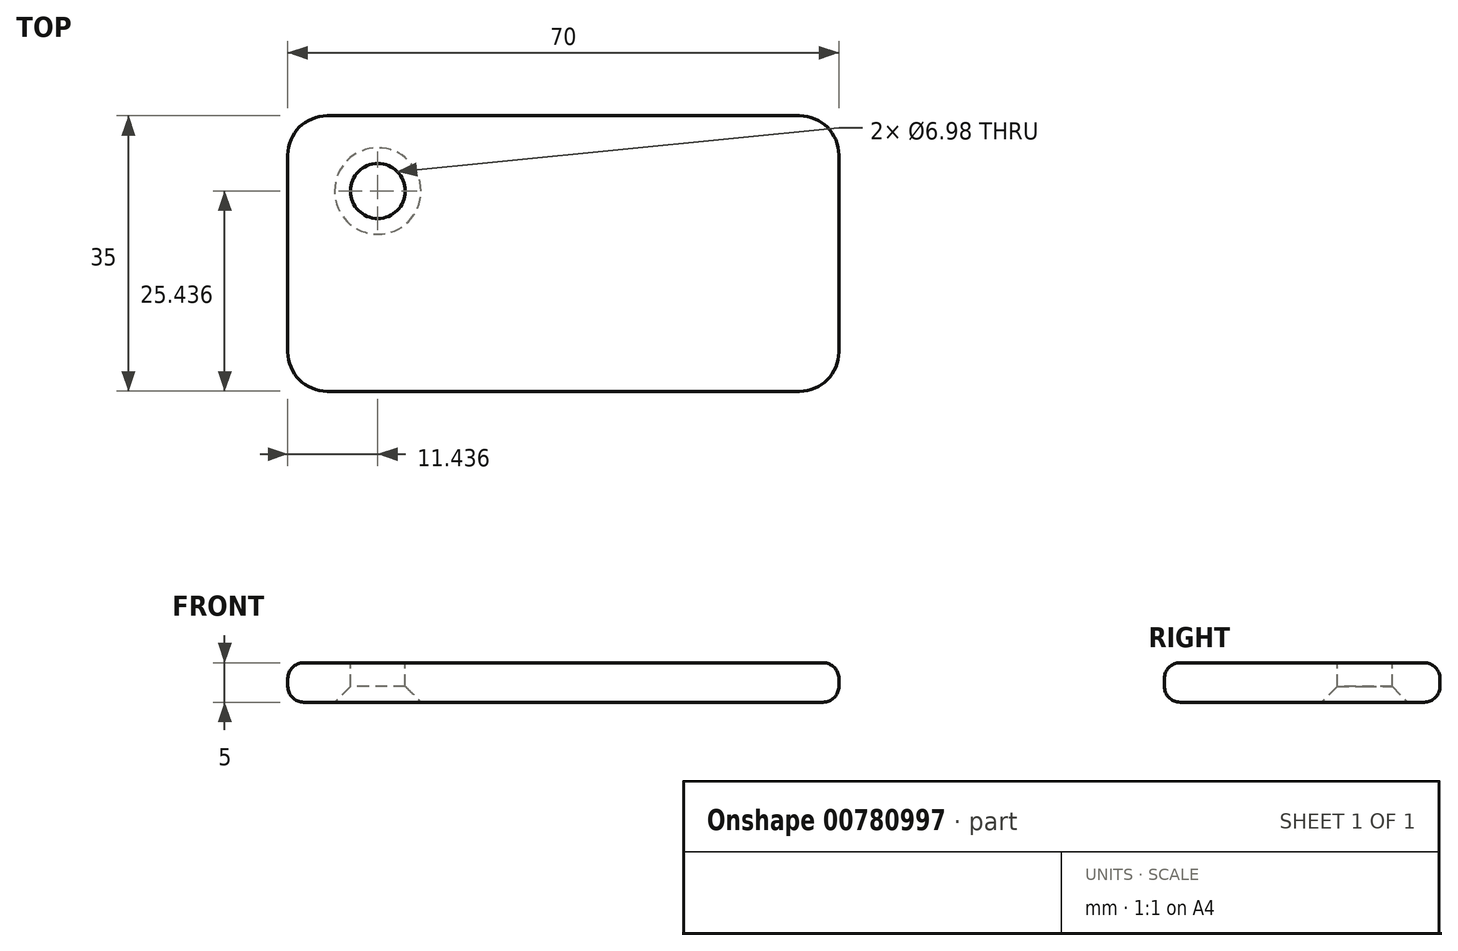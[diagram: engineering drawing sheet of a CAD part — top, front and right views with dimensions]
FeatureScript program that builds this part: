
annotation { "Feature Type Name" : "Feature", "Feature Type Description" : "" }
export const myFeature = defineFeature(function(context is Context, id is Id, definition is map)
    precondition{}
    {
        {
            var Q0;
            Q0=qCreatedBy(makeId("Top.planeOp"),FACE);
            var sketch = newSketch(context, id + "F0", { "sketchPlane" : qUnion([Q0])});
            skLineSegment(sketch, "E0.bottom", {"start": v(15.7, -5.3) * mm, "end": v(-44.3, -5.3) * mm});
            skLineSegment(sketch, "E0.top", {"start": v(15.7, -40.3) * mm, "end": v(-44.3, -40.3) * mm});
            skLineSegment(sketch, "E0.left", {"start": v(20.7, -10.3) * mm, "end": v(20.7, -35.3) * mm});
            skLineSegment(sketch, "E0.right", {"start": v(-49.3, -10.3) * mm, "end": v(-49.3, -35.3) * mm});
            skPoint(sketch, "E0.middle", {"position": v(-14.3, -22.8) * mm});
            skPoint(sketch, "E1.right.end.orphan", {"position": v(-3.57, 0) * mm});
            skPoint(sketch, "E2.visualSharp", {"position": v(20.7, -5.3) * mm});
            skArc(sketch, "E2.filletArc", {"start": v(20.7, -10.3) * mm, "mid": v(19.23, -6.77) * mm, "end": v(15.7, -5.3) * mm});
            skPoint(sketch, "E3.visualSharp", {"position": v(-49.3, -5.3) * mm});
            skArc(sketch, "E3.filletArc", {"start": v(-44.3, -5.3) * mm, "mid": v(-47.84, -6.77) * mm, "end": v(-49.3, -10.3) * mm});
            skPoint(sketch, "E4.visualSharp", {"position": v(-49.3, -40.3) * mm});
            skArc(sketch, "E4.filletArc", {"start": v(-49.3, -35.3) * mm, "mid": v(-47.84, -38.84) * mm, "end": v(-44.3, -40.3) * mm});
            skPoint(sketch, "E5.visualSharp", {"position": v(20.7, -40.3) * mm});
            skArc(sketch, "E5.filletArc", {"start": v(15.7, -40.3) * mm, "mid": v(19.23, -38.84) * mm, "end": v(20.7, -35.3) * mm});
            skSolve(sketch);
        }
        {
            var Q0;
            Q0=makeQuery(id+"F0.imprint","IMPRINT",FACE,{"disambiguationData":[TD([[makeQuery(id+"F0.imprint","IMPRINT",EDGE,{"derivedFrom":sQuery(id+"F0.wireOp",EDGE,"E0.bottom")}),1.0]])]});
            extrude(context, id + "F1", {"entities" : qUnion([Q0]), "depth" : 5 * mm, "offsetDistance" : 25 * mm});
        }
        {
            var Q0;
            Q0=makeQuery(id+"F1.opExtrude","CAP_EDGE",EDGE,{"disambiguationData":[OSD([sQuery(id+"F0.wireOp",EDGE,"E0.right")])],"isStart":false});
            var Q1;
            Q1=makeQuery(id+"F1.opExtrude","CAP_EDGE",EDGE,{"disambiguationData":[OSD([sQuery(id+"F0.wireOp",EDGE,"E0.right")])],"isStart":true});
            fillet(context, id + "F2", {"entities" : qUnion([Q0, Q1]), "radius" : 2 * mm, "tangentPropagation" : true, "allowEdgeOverflow" : false});
        }
        {
            var Q0;
            Q0=makeQuery(id+"F1.opExtrude","CAP_FACE",FACE,{"disambiguationData":[OSD([sQuery(id+"F0.wireOp",EDGE,"E0.bottom"),sQuery(id+"F0.wireOp",EDGE,"E0.top"),sQuery(id+"F0.wireOp",EDGE,"E0.left"),sQuery(id+"F0.wireOp",EDGE,"E0.right"),sQuery(id+"F0.wireOp",EDGE,"E2.filletArc"),sQuery(id+"F0.wireOp",EDGE,"E3.filletArc"),sQuery(id+"F0.wireOp",EDGE,"E4.filletArc"),sQuery(id+"F0.wireOp",EDGE,"E5.filletArc")])],"isStart":false});
            var sketch = newSketch(context, id + "F3", { "sketchPlane" : qUnion([Q0])});
            skCircle(sketch, "E6", {"center": v(-37.87, -14.86) * mm, "radius": 3.49 * mm});
            skSolve(sketch);
        }
        {
            var Q0;
            Q0=makeQuery(id+"F3.imprint","IMPRINT",FACE,{"disambiguationData":[TD([[makeQuery(id+"F3.imprint","IMPRINT",EDGE,{"derivedFrom":sQuery(id+"F3.wireOp",EDGE,"E6")}),1.0]])]});
            extrude(context, id + "F4", {"entities" : qUnion([Q0]), "operationType" : NewBodyOperationType.REMOVE, "oppositeDirection" : true, "depth" : 25 * mm, "offsetDistance" : 25 * mm});
        }
        {
            var Q0;
            Q0=makeQuery(id+"F4.boolean.opBoolean","COPY",EDGE,{"derivedFrom":makeQuery(id+"F4.opExtrude","CAP_EDGE",EDGE,{"disambiguationData":[OSD([sQuery(id+"F3.wireOp",EDGE,"E6")])],"isStart":true})});
            var Q1;
            Q1=makeQuery(id+"F4.boolean.opBoolean","INTERSECT",EDGE,{"derivedFrom":[makeQuery(id+"F1.opExtrude","CAP_FACE",FACE,{"disambiguationData":[OSD([sQuery(id+"F0.wireOp",EDGE,"E0.bottom"),sQuery(id+"F0.wireOp",EDGE,"E0.top"),sQuery(id+"F0.wireOp",EDGE,"E0.left"),sQuery(id+"F0.wireOp",EDGE,"E0.right"),sQuery(id+"F0.wireOp",EDGE,"E2.filletArc"),sQuery(id+"F0.wireOp",EDGE,"E3.filletArc"),sQuery(id+"F0.wireOp",EDGE,"E4.filletArc"),sQuery(id+"F0.wireOp",EDGE,"E5.filletArc")])],"isStart":true}),makeQuery(id+"F4.opExtrude","SWEPT_FACE",FACE,{"disambiguationData":[OSD([sQuery(id+"F3.wireOp",EDGE,"E6")])]})]});
            chamfer(context, id + "F5", {"entities" : qUnion([Q0, Q1]), "width" : 2 * mm, "tangentPropagation" : true});
        }
    });
